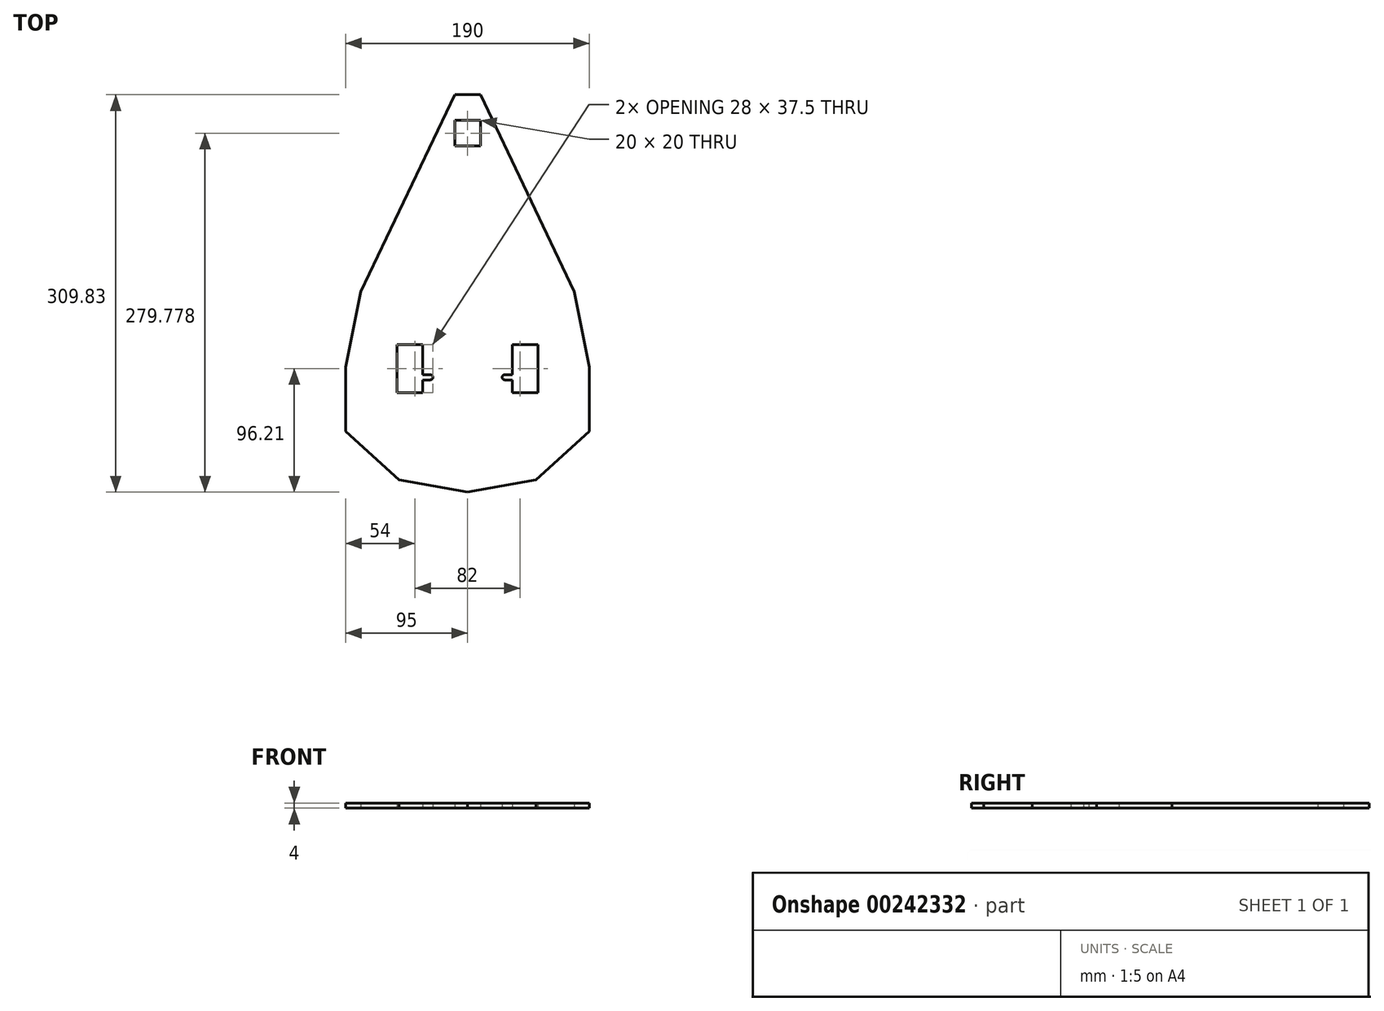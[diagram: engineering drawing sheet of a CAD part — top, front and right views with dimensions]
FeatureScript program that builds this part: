
annotation { "Feature Type Name" : "Feature", "Feature Type Description" : "" }
export const myFeature = defineFeature(function(context is Context, id is Id, definition is map)
    precondition{}
    {
        {
            var Q0;
            Q0=qCreatedBy(makeId("Top.planeOp"),FACE);
            var sketch = newSketch(context, id + "F0", { "sketchPlane" : qUnion([Q0])});
            skLineSegment(sketch, "E0", {"start": v(-55, 17.5) * mm, "end": v(-55, -20) * mm});
            skLineSegment(sketch, "E1", {"start": v(-55, -20) * mm, "end": v(-35, -20) * mm});
            skLineSegment(sketch, "E2", {"start": v(-35, -20) * mm, "end": v(-35, 17.5) * mm});
            skLineSegment(sketch, "E3", {"start": v(-35, 17.5) * mm, "end": v(-55, 17.5) * mm});
            skLineSegment(sketch, "E4", {"start": v(35, 17.5) * mm, "end": v(35, -20) * mm});
            skLineSegment(sketch, "E5", {"start": v(35, -20) * mm, "end": v(55, -20) * mm});
            skLineSegment(sketch, "E6", {"start": v(55, -20) * mm, "end": v(55, 17.5) * mm});
            skLineSegment(sketch, "E7", {"start": v(55, 17.5) * mm, "end": v(35, 17.5) * mm});
            skLineSegment(sketch, "E8", {"start": v(-95, 0) * mm, "end": v(-83.16, 58.82) * mm});
            skLineSegment(sketch, "E9", {"start": v(83.16, 58.82) * mm, "end": v(95, 0) * mm});
            skLineSegment(sketch, "E10", {"start": v(95, 0) * mm, "end": v(95, -50) * mm});
            skLineSegment(sketch, "E11", {"start": v(-95, -50) * mm, "end": v(-95, 0) * mm});
            skLineSegment(sketch, "E12", {"start": v(-95, -50) * mm, "end": v(-53.4, -87.9) * mm});
            skLineSegment(sketch, "E13", {"start": v(-53.4, -87.9) * mm, "end": v(0, -97.46) * mm});
            skLineSegment(sketch, "E14", {"start": v(53.4, -87.9) * mm, "end": v(95, -50) * mm});
            skLineSegment(sketch, "E15", {"start": v(53.4, -87.9) * mm, "end": v(0, -97.46) * mm});
            skLineSegment(sketch, "E16", {"start": v(-10, 212.37) * mm, "end": v(10, 212.37) * mm});
            skLineSegment(sketch, "E17", {"start": v(10, 212.37) * mm, "end": v(83.16, 58.82) * mm});
            skLineSegment(sketch, "E18", {"start": v(-10, 212.37) * mm, "end": v(-83.16, 58.82) * mm});
            skLineSegment(sketch, "E19", {"start": v(-10, 192.32) * mm, "end": v(10, 192.32) * mm});
            skLineSegment(sketch, "E20", {"start": v(10, 192.32) * mm, "end": v(10, 172.32) * mm});
            skLineSegment(sketch, "E21", {"start": v(10, 172.32) * mm, "end": v(-10, 172.32) * mm});
            skLineSegment(sketch, "E22", {"start": v(-10, 172.32) * mm, "end": v(-10, 192.32) * mm});
            skCircle(sketch, "E23", {"center": v(-29, -8) * mm, "radius": 2 * mm});
            skCircle(sketch, "E24", {"center": v(29, -8) * mm, "radius": 2 * mm});
            skLineSegment(sketch, "E25", {"start": v(-29, -10) * mm, "end": v(-35, -10) * mm});
            skLineSegment(sketch, "E26", {"start": v(-29, -6) * mm, "end": v(-35, -6) * mm});
            skLineSegment(sketch, "E27", {"start": v(-29, -10) * mm, "end": v(-29, -6) * mm});
            skArc(sketch, "E28", {"start": v(-29, -10) * mm, "mid": v(-27, -8) * mm, "end": v(-29, -6) * mm});
            skLineSegment(sketch, "E29", {"start": v(29, -6) * mm, "end": v(35, -6) * mm});
            skLineSegment(sketch, "E30", {"start": v(29, -10) * mm, "end": v(35, -10) * mm});
            skSolve(sketch);
        }
        {
            var Q0;
            Q0=makeQuery(id+"F0.imprint","IMPRINT",FACE,{"disambiguationData":[TD([[makeQuery(id+"F0.imprint","IMPRINT",EDGE,{"derivedFrom":sQuery(id+"F0.wireOp",EDGE,"E0")}),-1.0]])]});
            extrude(context, id + "F1", {"entities" : qUnion([Q0]), "depth" : 4 * mm});
        }
    });
